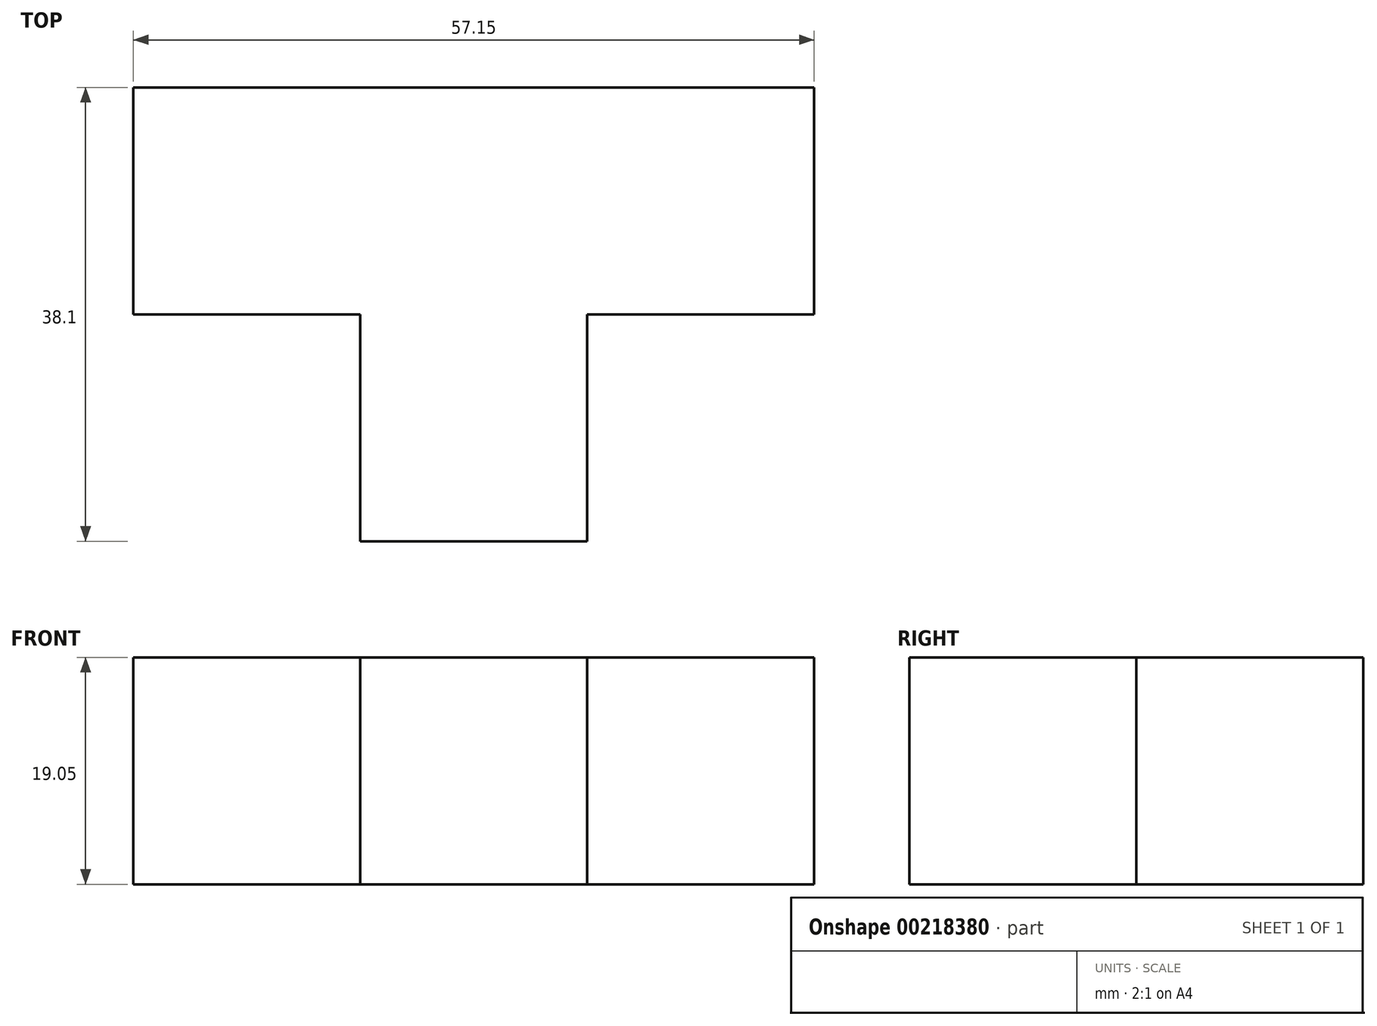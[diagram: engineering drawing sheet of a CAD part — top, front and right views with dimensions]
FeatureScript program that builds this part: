
annotation { "Feature Type Name" : "Feature", "Feature Type Description" : "" }
export const myFeature = defineFeature(function(context is Context, id is Id, definition is map)
    precondition{}
    {
        {
            var Q0;
            Q0=qCreatedBy(makeId("Front.planeOp"),FACE);
            var sketch = newSketch(context, id + "F0", { "sketchPlane" : qUnion([Q0])});
            skLineSegment(sketch, "E0.bottom", {"start": v(-61.04, 42.83) * mm, "end": v(-41.99, 42.83) * mm});
            skLineSegment(sketch, "E0.top", {"start": v(-61.04, 23.78) * mm, "end": v(-41.99, 23.78) * mm});
            skLineSegment(sketch, "E0.left", {"start": v(-61.04, 42.83) * mm, "end": v(-61.04, 23.78) * mm});
            skLineSegment(sketch, "E0.right", {"start": v(-41.99, 42.83) * mm, "end": v(-41.99, 23.78) * mm});
            skLineSegment(sketch, "E1.bottom", {"start": v(-22.94, 42.83) * mm, "end": v(-41.99, 42.83) * mm});
            skLineSegment(sketch, "E1.top", {"start": v(-22.94, 23.78) * mm, "end": v(-41.99, 23.78) * mm});
            skLineSegment(sketch, "E1.left", {"start": v(-22.94, 42.83) * mm, "end": v(-22.94, 23.78) * mm});
            skLineSegment(sketch, "E2.bottom", {"start": v(-3.89, 42.83) * mm, "end": v(-22.94, 42.83) * mm});
            skLineSegment(sketch, "E2.top", {"start": v(-3.89, 23.78) * mm, "end": v(-22.94, 23.78) * mm});
            skLineSegment(sketch, "E2.left", {"start": v(-3.89, 42.83) * mm, "end": v(-3.89, 23.78) * mm});
            skLineSegment(sketch, "E3.bottom", {"start": v(-41.99, 23.78) * mm, "end": v(-22.94, 23.78) * mm});
            skLineSegment(sketch, "E3.top", {"start": v(-41.99, 4.73) * mm, "end": v(-22.94, 4.73) * mm});
            skLineSegment(sketch, "E3.left", {"start": v(-41.99, 23.78) * mm, "end": v(-41.99, 4.73) * mm});
            skLineSegment(sketch, "E3.right", {"start": v(-22.94, 23.78) * mm, "end": v(-22.94, 4.73) * mm});
            skLineSegment(sketch, "E4.bottom", {"start": v(-22.94, 23.78) * mm, "end": v(-3.89, 23.78) * mm});
            skLineSegment(sketch, "E4.top", {"start": v(-22.94, 4.73) * mm, "end": v(-3.89, 4.73) * mm});
            skLineSegment(sketch, "E4.right", {"start": v(-3.89, 23.78) * mm, "end": v(-3.89, 4.73) * mm});
            skSolve(sketch);
        }
        {
            var Q0;
            Q0=makeQuery(id+"F0.imprint","IMPRINT",FACE,{"disambiguationData":[TD([[makeQuery(id+"F0.imprint","IMPRINT",EDGE,{"derivedFrom":sQuery(id+"F0.wireOp",EDGE,"E0.bottom")}),-1.0]])]});
            var Q1;
            Q1=makeQuery(id+"F0.imprint","IMPRINT",FACE,{"disambiguationData":[TD([[makeQuery(id+"F0.imprint","IMPRINT",EDGE,{"derivedFrom":sQuery(id+"F0.wireOp",EDGE,"E1.bottom")}),1.0]])]});
            var Q2;
            Q2=makeQuery(id+"F0.imprint","IMPRINT",FACE,{"disambiguationData":[TD([[makeQuery(id+"F0.imprint","IMPRINT",EDGE,{"derivedFrom":sQuery(id+"F0.wireOp",EDGE,"E2.bottom")}),1.0]])]});
            var Q3;
            Q3=makeQuery(id+"F0.imprint","IMPRINT",FACE,{"disambiguationData":[TD([[makeQuery(id+"F0.imprint","IMPRINT",EDGE,{"derivedFrom":sQuery(id+"F0.wireOp",EDGE,"E4.bottom")}),-1.0]])]});
            var Q4;
            Q4=makeQuery(id+"F0.imprint","IMPRINT",FACE,{"disambiguationData":[TD([[makeQuery(id+"F0.imprint","IMPRINT",EDGE,{"derivedFrom":sQuery(id+"F0.wireOp",EDGE,"E3.bottom")}),-1.0]])]});
            extrude(context, id + "F1", {"entities" : qUnion([Q0, Q1, Q2, Q3, Q4]), "depth" : 19.05 * mm});
        }
        {
            var Q0;
            Q0=makeQuery(id+"F1.opExtrude","CAP_FACE",FACE,{"disambiguationData":[OSD([sQuery(id+"F0.wireOp",EDGE,"E0.bottom"),sQuery(id+"F0.wireOp",EDGE,"E0.top"),sQuery(id+"F0.wireOp",EDGE,"E0.left"),sQuery(id+"F0.wireOp",EDGE,"E1.bottom"),sQuery(id+"F0.wireOp",EDGE,"E2.bottom"),sQuery(id+"F0.wireOp",EDGE,"E2.left"),sQuery(id+"F0.wireOp",EDGE,"E3.top"),sQuery(id+"F0.wireOp",EDGE,"E3.left"),sQuery(id+"F0.wireOp",EDGE,"E4.top"),sQuery(id+"F0.wireOp",EDGE,"E4.right")])],"isStart":false});
            var sketch = newSketch(context, id + "F2", { "sketchPlane" : qUnion([Q0])});
            skLineSegment(sketch, "E5.bottom", {"start": v(-41.99, 23.78) * mm, "end": v(-22.94, 23.78) * mm});
            skLineSegment(sketch, "E5.top", {"start": v(-41.99, 42.83) * mm, "end": v(-22.94, 42.83) * mm});
            skLineSegment(sketch, "E5.left", {"start": v(-41.99, 23.78) * mm, "end": v(-41.99, 42.83) * mm});
            skLineSegment(sketch, "E5.right", {"start": v(-22.94, 23.78) * mm, "end": v(-22.94, 42.83) * mm});
            skSolve(sketch);
        }
        {
            var Q0;
            Q0=makeQuery(id+"F2.imprint","IMPRINT",FACE,{"disambiguationData":[TD([[makeQuery(id+"F2.imprint","IMPRINT",EDGE,{"derivedFrom":sQuery(id+"F2.wireOp",EDGE,"E5.bottom")}),1.0]])]});
            extrude(context, id + "F3", {"entities" : qUnion([Q0]), "operationType" : NewBodyOperationType.ADD, "depth" : 19.05 * mm});
        }
    });
